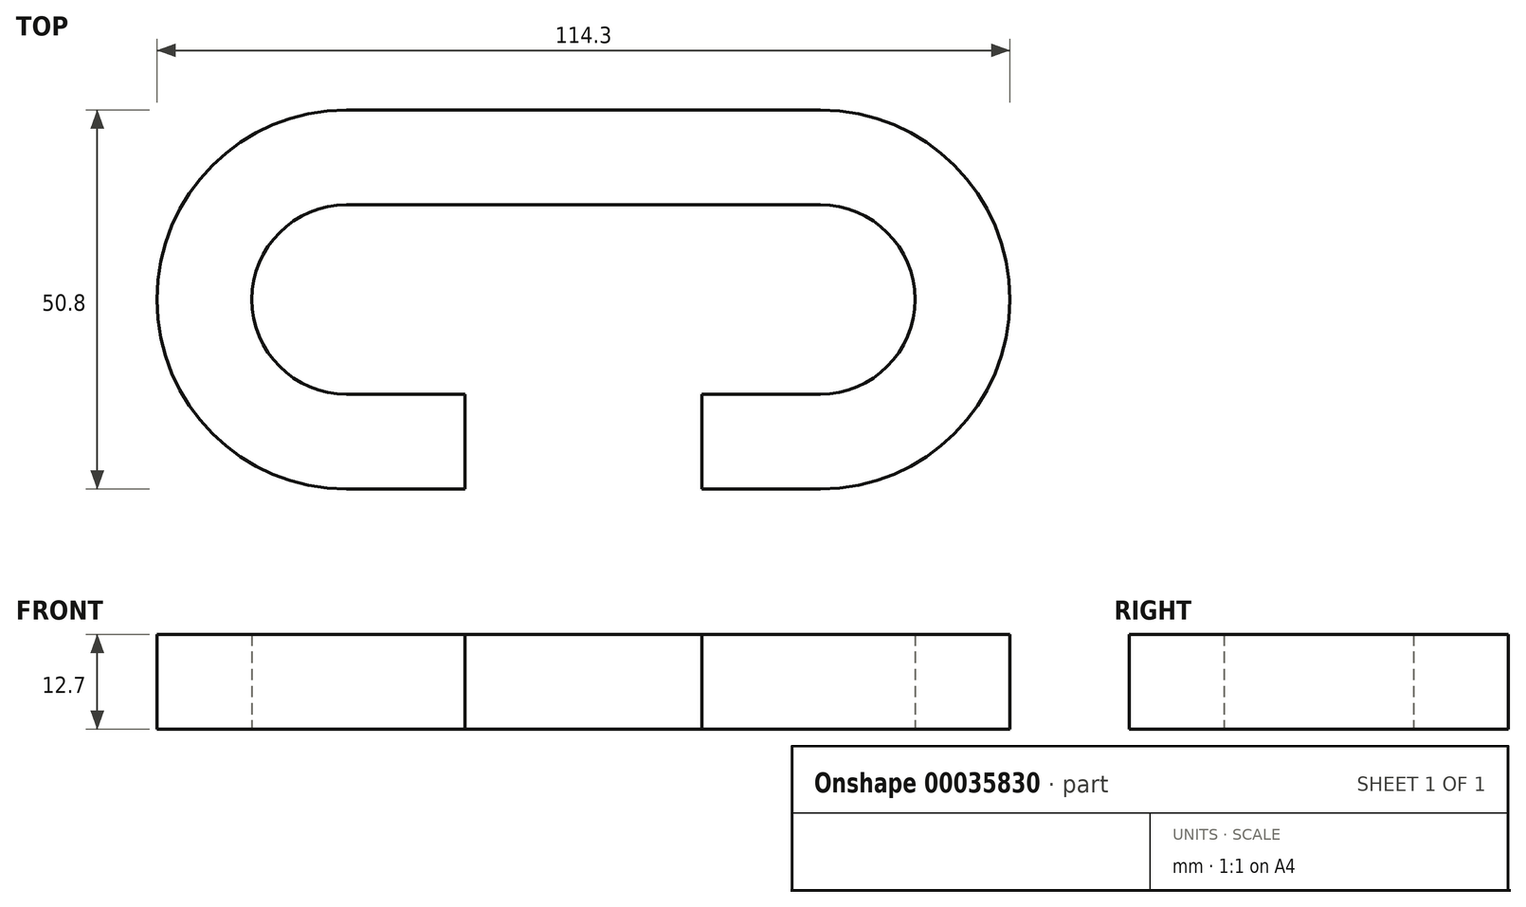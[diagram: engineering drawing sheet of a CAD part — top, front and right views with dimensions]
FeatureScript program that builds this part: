
annotation { "Feature Type Name" : "Feature", "Feature Type Description" : "" }
export const myFeature = defineFeature(function(context is Context, id is Id, definition is map)
    precondition{}
    {
        {
            var Q0;
            Q0=qCreatedBy(makeId("Top.planeOp"),FACE);
            var sketch = newSketch(context, id + "F0", { "sketchPlane" : qUnion([Q0])});
            skLineSegment(sketch, "E0.bottom", {"start": v(0, 12.7) * mm, "end": v(0, 12.7) * mm});
            skLineSegment(sketch, "E0.top", {"start": v(0, -12.7) * mm, "end": v(0, -12.7) * mm});
            skLineSegment(sketch, "E0.right", {"start": v(0, 12.7) * mm, "end": v(0, -12.7) * mm});
            skCircle(sketch, "E1", {"center": v(0, 0) * mm, "radius": 12.7 * mm});
            skLineSegment(sketch, "E2", {"start": v(0, 12.7) * mm, "end": v(-63.5, 12.7) * mm});
            skLineSegment(sketch, "E3", {"start": v(0, -12.7) * mm, "end": v(-63.5, -12.7) * mm});
            skCircle(sketch, "E4", {"center": v(-63.5, 0) * mm, "radius": 12.7 * mm});
            skLineSegment(sketch, "E5", {"start": v(-63.5, 12.7) * mm, "end": v(-63.5, 0) * mm});
            skPoint(sketch, "E6.center.orphan", {"position": v(-31.75, -12.7) * mm});
            skLineSegment(sketch, "E7", {"start": v(-63.5, 0) * mm, "end": v(-63.5, -12.7) * mm});
            skCircle(sketch, "E8", {"center": v(-63.5, 0) * mm, "radius": 25.4 * mm});
            skCircle(sketch, "E9", {"center": v(0, 0) * mm, "radius": 25.4 * mm});
            skLineSegment(sketch, "E10", {"start": v(-63.5, 25.4) * mm, "end": v(0, 25.4) * mm});
            skLineSegment(sketch, "E11", {"start": v(0, -25.4) * mm, "end": v(-63.5, -25.4) * mm});
            skLineSegment(sketch, "E12", {"start": v(-47.62, -12.7) * mm, "end": v(-47.62, -25.4) * mm});
            skLineSegment(sketch, "E13", {"start": v(-15.88, -12.7) * mm, "end": v(-15.88, -25.4) * mm});
            skLineSegment(sketch, "E14", {"start": v(-47.62, -19.05) * mm, "end": v(-15.88, -19.05) * mm});
            skPoint(sketch, "E15", {"position": v(-31.75, -19.05) * mm});
            skSolve(sketch);
        }
        {
            var Q0;
            {var subQ1=sQuery(id+"F0.wireOp",EDGE,"E9");var subQ3=sQuery(id+"F0.wireOp",EDGE,"E11");var subQ5=makeQuery(id+"F0.imprint","INTERSECT",VERTEX,{"derivedFrom":[subQ1,subQ3]});Q0=makeQuery(id+"F0.imprint","IMPRINT",FACE,{"disambiguationData":[TD([[makeQuery(id+"F0.imprint","IMPRINT",EDGE,{"disambiguationData":[TD([[subQ5,1.0]])],"derivedFrom":subQ1}),-1.0]])]});}
            var Q1;
            {var subQ1=sQuery(id+"F0.wireOp",EDGE,"E9");var subQ7=makeQuery(id+"F0.imprint","INTERSECT",VERTEX,{"derivedFrom":[subQ1,sQuery(id+"F0.wireOp",EDGE,"E10")]});Q1=makeQuery(id+"F0.imprint","IMPRINT",FACE,{"disambiguationData":[TD([[makeQuery(id+"F0.imprint","IMPRINT",EDGE,{"disambiguationData":[TD([[subQ7,-1.0]])],"derivedFrom":subQ1}),1.0]])]});}
            var Q2;
            {var subQ0=sQuery(id+"F0.wireOp",EDGE,"E10");Q2=makeQuery(id+"F0.imprint","IMPRINT",FACE,{"disambiguationData":[TD([[makeQuery(id+"F0.imprint","IMPRINT",EDGE,{"derivedFrom":subQ0}),-1.0]])]});}
            var Q3;
            {var subQ1=sQuery(id+"F0.wireOp",EDGE,"E8");var subQ7=makeQuery(id+"F0.imprint","INTERSECT",VERTEX,{"derivedFrom":[subQ1,sQuery(id+"F0.wireOp",EDGE,"E10")]});Q3=makeQuery(id+"F0.imprint","IMPRINT",FACE,{"disambiguationData":[TD([[makeQuery(id+"F0.imprint","IMPRINT",EDGE,{"disambiguationData":[TD([[subQ7,1.0]])],"derivedFrom":subQ1}),1.0]])]});}
            var Q4;
            {var subQ0=sQuery(id+"F0.wireOp",EDGE,"E11");var subQ3=sQuery(id+"F0.wireOp",EDGE,"E8");var subQ4=makeQuery(id+"F0.imprint","INTERSECT",VERTEX,{"derivedFrom":[subQ3,subQ0]});Q4=makeQuery(id+"F0.imprint","IMPRINT",FACE,{"disambiguationData":[TD([[makeQuery(id+"F0.imprint","IMPRINT",EDGE,{"disambiguationData":[TD([[subQ4,-1.0]])],"derivedFrom":subQ3}),-1.0]])]});}
            extrude(context, id + "F1", {"entities" : qUnion([Q0, Q1, Q2, Q3, Q4]), "depth" : 12.7 * mm});
        }
    });
